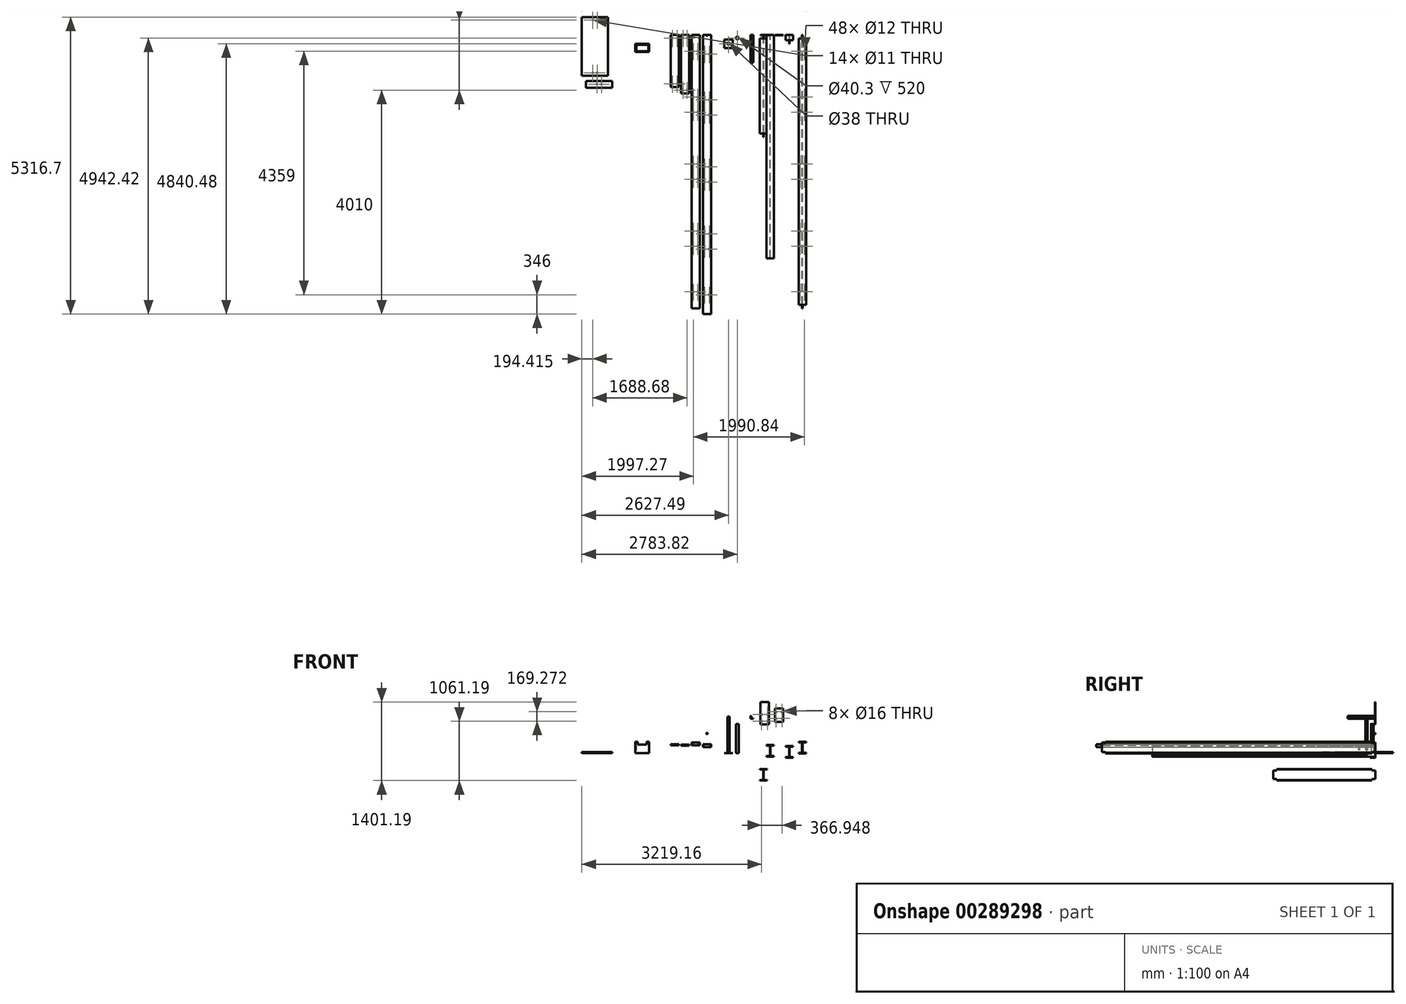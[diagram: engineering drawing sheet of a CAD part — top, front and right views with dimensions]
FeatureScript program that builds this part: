
annotation { "Feature Type Name" : "Feature", "Feature Type Description" : "" }
export const myFeature = defineFeature(function(context is Context, id is Id, definition is map)
    precondition{}
    {
        {
            var Q0;
            Q0=qCreatedBy(makeId("Front.planeOp"),FACE);
            var sketch = newSketch(context, id + "F0", { "sketchPlane" : qUnion([Q0])});
            skLineSegment(sketch, "E0", {"start": v(-21.34, 72.01) * mm, "end": v(112.46, 72.01) * mm});
            skLineSegment(sketch, "E1", {"start": v(-21.34, 72.01) * mm, "end": v(-21.34, 62.41) * mm});
            skLineSegment(sketch, "E2", {"start": v(112.46, 72.01) * mm, "end": v(112.46, 62.41) * mm});
            skLineSegment(sketch, "E3", {"start": v(-21.34, 62.41) * mm, "end": v(42.4, 62.41) * mm});
            skLineSegment(sketch, "E4", {"start": v(112.46, 62.41) * mm, "end": v(48.7, 62.41) * mm});
            skLineSegment(sketch, "E5", {"start": v(42.4, -125.19) * mm, "end": v(-21.34, -125.19) * mm});
            skLineSegment(sketch, "E6", {"start": v(-21.34, -125.19) * mm, "end": v(-21.34, -134.79) * mm});
            skLineSegment(sketch, "E7", {"start": v(-21.34, -134.79) * mm, "end": v(112.46, -134.79) * mm});
            skLineSegment(sketch, "E8", {"start": v(112.46, -134.79) * mm, "end": v(112.46, -125.19) * mm});
            skLineSegment(sketch, "E9", {"start": v(112.46, -125.19) * mm, "end": v(48.7, -125.19) * mm});
            skLineSegment(sketch, "E10", {"start": v(42.4, 62.41) * mm, "end": v(42.4, 54.81) * mm});
            skLineSegment(sketch, "E11", {"start": v(42.4, 54.81) * mm, "end": v(42.4, -117.59) * mm});
            skLineSegment(sketch, "E12", {"start": v(42.4, -117.59) * mm, "end": v(42.4, -125.19) * mm});
            skLineSegment(sketch, "E13", {"start": v(48.7, 62.41) * mm, "end": v(48.7, 54.81) * mm});
            skLineSegment(sketch, "E14", {"start": v(48.7, 54.81) * mm, "end": v(48.7, -117.59) * mm});
            skLineSegment(sketch, "E15", {"start": v(48.7, -117.59) * mm, "end": v(48.7, -125.19) * mm});
            skArc(sketch, "E16", {"start": v(42.4, 54.81) * mm, "mid": v(40.18, 60.19) * mm, "end": v(34.8, 62.41) * mm});
            skArc(sketch, "E17", {"start": v(56.58, 62.41) * mm, "mid": v(51.03, 60.28) * mm, "end": v(48.7, 54.81) * mm});
            skArc(sketch, "E18", {"start": v(42.4, -117.59) * mm, "mid": v(40.18, -122.96) * mm, "end": v(34.8, -125.19) * mm});
            skArc(sketch, "E19", {"start": v(48.7, -117.59) * mm, "mid": v(51.13, -123.16) * mm, "end": v(56.86, -125.19) * mm});
            skLineSegment(sketch, "E20", {"start": v(56.58, 62.41) * mm, "end": v(112.46, 62.41) * mm});
            skSolve(sketch);
        }
        {
            var Q0;
            Q0=qCreatedBy(makeId("Top.planeOp"),FACE);
            var sketch = newSketch(context, id + "F1", { "sketchPlane" : qUnion([Q0])});
            skLineSegment(sketch, "E21.bottom", {"start": v(-453.65, -234.52) * mm, "end": v(-603.65, -234.52) * mm});
            skLineSegment(sketch, "E21.top", {"start": v(-453.65, -84.52) * mm, "end": v(-603.65, -84.52) * mm});
            skLineSegment(sketch, "E21.left", {"start": v(-453.65, -234.52) * mm, "end": v(-453.65, -84.52) * mm});
            skLineSegment(sketch, "E21.right", {"start": v(-603.65, -234.52) * mm, "end": v(-603.65, -84.52) * mm});
            skPoint(sketch, "E21.middle", {"position": v(-528.65, -159.52) * mm});
            skCircle(sketch, "E22", {"center": v(-528.65, -159.52) * mm, "radius": 19 * mm});
            skSolve(sketch);
        }
        {
            var Q0;
            Q0=makeQuery(id+"F1.imprint","IMPRINT",FACE,{"disambiguationData":[TD([[makeQuery(id+"F1.imprint","IMPRINT",EDGE,{"derivedFrom":sQuery(id+"F1.wireOp",EDGE,"E22")}),1.0]])]});
            extrude(context, id + "F2", {"entities" : qUnion([Q0]), "depth" : 650 * mm});
        }
        {
            var Q0;
            Q0=qSketchRegion(id+"F1",true);
            extrude(context, id + "F3", {"entities" : qUnion([Q0]), "oppositeDirection" : true, "depth" : 4 * mm});
        }
        {
            var Q0;
            Q0=qCreatedBy(makeId("Top.planeOp"),FACE);
            var sketch = newSketch(context, id + "F4", { "sketchPlane" : qUnion([Q0])});
            skCircle(sketch, "E23", {"center": v(-372.32, -57.58) * mm, "radius": 24.15 * mm});
            skCircle(sketch, "E24.0", {"center": v(-372.32, -57.58) * mm, "radius": 20.15 * mm});
            skSolve(sketch);
        }
        {
            var Q0;
            Q0=makeQuery(id+"F4.imprint","IMPRINT",FACE,{"disambiguationData":[TD([[makeQuery(id+"F4.imprint","IMPRINT",EDGE,{"derivedFrom":sQuery(id+"F4.wireOp",EDGE,"E23")}),1.0]])]});
            extrude(context, id + "F5", {"entities" : qUnion([Q0]), "depth" : 520 * mm});
        }
        {
            var Q0;
            Q0=makeQuery(id+"F0.imprint","IMPRINT",FACE,{"disambiguationData":[TD([[makeQuery(id+"F0.imprint","IMPRINT",EDGE,{"derivedFrom":sQuery(id+"F0.wireOp",EDGE,"E0")}),-1.0]])]});
            var sketch = newSketch(context, id + "F6", { "sketchPlane" : qUnion([Q0])});
            skLineSegment(sketch, "E25", {"start": v(148.56, 141.3) * mm, "end": v(282.36, 141.3) * mm});
            skLineSegment(sketch, "E26", {"start": v(148.56, 141.3) * mm, "end": v(148.56, 131.7) * mm});
            skLineSegment(sketch, "E27", {"start": v(282.36, 141.3) * mm, "end": v(282.36, 131.7) * mm});
            skLineSegment(sketch, "E28", {"start": v(148.56, 131.7) * mm, "end": v(212.04, 131.7) * mm});
            skLineSegment(sketch, "E29", {"start": v(282.36, 131.7) * mm, "end": v(218.89, 131.7) * mm});
            skLineSegment(sketch, "E30", {"start": v(212.04, -55.9) * mm, "end": v(148.56, -55.9) * mm});
            skLineSegment(sketch, "E31", {"start": v(148.56, -55.9) * mm, "end": v(148.56, -65.5) * mm});
            skLineSegment(sketch, "E32", {"start": v(148.56, -65.5) * mm, "end": v(282.36, -65.5) * mm});
            skLineSegment(sketch, "E33", {"start": v(282.36, -65.5) * mm, "end": v(282.36, -55.9) * mm});
            skLineSegment(sketch, "E34", {"start": v(282.36, -55.9) * mm, "end": v(218.89, -55.9) * mm});
            skLineSegment(sketch, "E35", {"start": v(212.04, 131.7) * mm, "end": v(212.04, 124.1) * mm});
            skLineSegment(sketch, "E36", {"start": v(212.04, 124.1) * mm, "end": v(212.04, -48.3) * mm});
            skLineSegment(sketch, "E37", {"start": v(212.04, -48.3) * mm, "end": v(212.04, -55.9) * mm});
            skLineSegment(sketch, "E38", {"start": v(218.89, 131.7) * mm, "end": v(218.89, 124.1) * mm});
            skLineSegment(sketch, "E39", {"start": v(218.89, 124.1) * mm, "end": v(218.89, -48.3) * mm});
            skLineSegment(sketch, "E40", {"start": v(218.89, -48.3) * mm, "end": v(218.89, -55.9) * mm});
            skArc(sketch, "E41", {"start": v(212.04, 124.1) * mm, "mid": v(209.81, 129.48) * mm, "end": v(204.44, 131.7) * mm});
            skArc(sketch, "E42", {"start": v(226.49, 131.7) * mm, "mid": v(221.11, 129.48) * mm, "end": v(218.89, 124.1) * mm});
            skArc(sketch, "E43", {"start": v(212.04, -48.3) * mm, "mid": v(209.81, -53.67) * mm, "end": v(204.44, -55.9) * mm});
            skArc(sketch, "E44", {"start": v(218.89, -48.3) * mm, "mid": v(221.11, -53.67) * mm, "end": v(226.49, -55.9) * mm});
            skLineSegment(sketch, "E45", {"start": v(226.49, 131.7) * mm, "end": v(282.36, 131.7) * mm});
            skSolve(sketch);
        }
        {
            var Q0;
            Q0=makeQuery(id+"F6.imprint","IMPRINT",FACE,{"disambiguationData":[TD([[makeQuery(id+"F6.imprint","IMPRINT",EDGE,{"derivedFrom":sQuery(id+"F6.wireOp",EDGE,"E25")}),-1.0]])]});
            var Q1;
            {var subQ0=sQuery(id+"F6.wireOp",EDGE,"E40");Q1=makeQuery(id+"F6.imprint","IMPRINT",FACE,{"disambiguationData":[TD([[makeQuery(id+"F6.imprint","IMPRINT",EDGE,{"derivedFrom":subQ0}),1.0]])]});}
            var Q2;
            {var subQ0=sQuery(id+"F6.wireOp",EDGE,"E37");Q2=makeQuery(id+"F6.imprint","IMPRINT",FACE,{"disambiguationData":[TD([[makeQuery(id+"F6.imprint","IMPRINT",EDGE,{"derivedFrom":subQ0}),-1.0]])]});}
            var Q3;
            Q3=makeQuery(id+"F6.imprint","IMPRINT",FACE,{"disambiguationData":[TD([[makeQuery(id+"F6.imprint","IMPRINT",EDGE,{"derivedFrom":sQuery(id+"F6.wireOp",EDGE,"E29")}),1.0]])]});
            var Q4;
            {var subQ0=sQuery(id+"F6.wireOp",EDGE,"E35");Q4=makeQuery(id+"F6.imprint","IMPRINT",FACE,{"disambiguationData":[TD([[makeQuery(id+"F6.imprint","IMPRINT",EDGE,{"derivedFrom":subQ0}),-1.0]])]});}
            extrude(context, id + "F7", {"entities" : qUnion([Q0, Q1, Q2, Q3, Q4]), "depth" : 4000 * mm});
        }
        {
            var Q0;
            Q0=qCreatedBy(makeId("Front.planeOp"),FACE);
            var sketch = newSketch(context, id + "F8", { "sketchPlane" : qUnion([Q0])});
            skLineSegment(sketch, "E46", {"start": v(-125.57, 662.13) * mm, "end": v(-125.57, 620.13) * mm});
            skLineSegment(sketch, "E47", {"start": v(-125.57, 620.13) * mm, "end": v(-83.57, 620.13) * mm});
            skLineSegment(sketch, "E48", {"start": v(-83.57, 620.13) * mm, "end": v(-83.57, 612.13) * mm});
            skLineSegment(sketch, "E49", {"start": v(-83.57, 612.13) * mm, "end": v(-133.57, 612.13) * mm});
            skLineSegment(sketch, "E50", {"start": v(-133.57, 612.13) * mm, "end": v(-133.57, 662.13) * mm});
            skLineSegment(sketch, "E51", {"start": v(-133.57, 662.13) * mm, "end": v(-125.57, 662.13) * mm});
            skSolve(sketch);
        }
        {
            var Q0;
            Q0=makeQuery(id+"F8.imprint","IMPRINT",FACE,{"disambiguationData":[TD([[makeQuery(id+"F8.imprint","IMPRINT",EDGE,{"derivedFrom":sQuery(id+"F8.wireOp",EDGE,"E46")}),-1.0]])]});
            extrude(context, id + "F9", {"entities" : qUnion([Q0]), "depth" : 500 * mm});
        }
        {
            var Q0;
            Q0=qCreatedBy(makeId("Front.planeOp"),FACE);
            var sketch = newSketch(context, id + "F10", { "sketchPlane" : qUnion([Q0])});
            skLineSegment(sketch, "E52", {"start": v(493.4, 124.28) * mm, "end": v(627.2, 124.28) * mm});
            skLineSegment(sketch, "E53", {"start": v(493.4, 124.28) * mm, "end": v(493.4, 114.68) * mm});
            skLineSegment(sketch, "E54", {"start": v(627.2, 124.28) * mm, "end": v(627.2, 114.68) * mm});
            skLineSegment(sketch, "E55", {"start": v(493.4, 114.68) * mm, "end": v(557.15, 114.68) * mm});
            skLineSegment(sketch, "E56", {"start": v(627.2, 114.68) * mm, "end": v(563.45, 114.68) * mm});
            skLineSegment(sketch, "E57", {"start": v(557.15, -72.92) * mm, "end": v(493.4, -72.92) * mm});
            skLineSegment(sketch, "E58", {"start": v(493.4, -72.92) * mm, "end": v(493.4, -82.52) * mm});
            skLineSegment(sketch, "E59", {"start": v(493.4, -82.52) * mm, "end": v(627.2, -82.52) * mm});
            skLineSegment(sketch, "E60", {"start": v(627.2, -82.52) * mm, "end": v(627.2, -72.92) * mm});
            skLineSegment(sketch, "E61", {"start": v(627.2, -72.92) * mm, "end": v(563.45, -72.92) * mm});
            skLineSegment(sketch, "E62", {"start": v(557.15, 114.68) * mm, "end": v(557.15, 107.08) * mm});
            skLineSegment(sketch, "E63", {"start": v(557.15, 107.08) * mm, "end": v(557.15, -65.32) * mm});
            skLineSegment(sketch, "E64", {"start": v(557.15, -65.32) * mm, "end": v(557.15, -72.92) * mm});
            skLineSegment(sketch, "E65", {"start": v(563.45, 114.68) * mm, "end": v(563.45, 107.08) * mm});
            skLineSegment(sketch, "E66", {"start": v(563.45, 107.08) * mm, "end": v(563.45, -65.32) * mm});
            skLineSegment(sketch, "E67", {"start": v(563.45, -65.32) * mm, "end": v(563.45, -72.92) * mm});
            skArc(sketch, "E68", {"start": v(557.15, 107.08) * mm, "mid": v(554.93, 112.46) * mm, "end": v(549.55, 114.68) * mm});
            skArc(sketch, "E69", {"start": v(571.33, 114.68) * mm, "mid": v(565.78, 112.55) * mm, "end": v(563.45, 107.08) * mm});
            skArc(sketch, "E70", {"start": v(557.15, -65.32) * mm, "mid": v(554.93, -70.7) * mm, "end": v(549.55, -72.92) * mm});
            skArc(sketch, "E71", {"start": v(563.45, -65.32) * mm, "mid": v(565.88, -70.89) * mm, "end": v(571.6, -72.92) * mm});
            skLineSegment(sketch, "E72", {"start": v(571.33, 114.68) * mm, "end": v(627.2, 114.68) * mm});
            skSolve(sketch);
        }
        {
            var Q0;
            Q0=makeQuery(id+"F10.imprint","IMPRINT",FACE,{"disambiguationData":[TD([[makeQuery(id+"F10.imprint","IMPRINT",EDGE,{"derivedFrom":sQuery(id+"F10.wireOp",EDGE,"E52")}),-1.0]])]});
            var Q1;
            {var subQ0=sQuery(id+"F10.wireOp",EDGE,"E64");Q1=makeQuery(id+"F10.imprint","IMPRINT",FACE,{"disambiguationData":[TD([[makeQuery(id+"F10.imprint","IMPRINT",EDGE,{"derivedFrom":subQ0}),-1.0]])]});}
            var Q2;
            {var subQ0=sQuery(id+"F10.wireOp",EDGE,"E67");Q2=makeQuery(id+"F10.imprint","IMPRINT",FACE,{"disambiguationData":[TD([[makeQuery(id+"F10.imprint","IMPRINT",EDGE,{"derivedFrom":subQ0}),1.0]])]});}
            var Q3;
            Q3=makeQuery(id+"F10.imprint","IMPRINT",FACE,{"disambiguationData":[TD([[makeQuery(id+"F10.imprint","IMPRINT",EDGE,{"derivedFrom":sQuery(id+"F10.wireOp",EDGE,"E56")}),1.0]])]});
            var Q4;
            {var subQ0=sQuery(id+"F10.wireOp",EDGE,"E62");Q4=makeQuery(id+"F10.imprint","IMPRINT",FACE,{"disambiguationData":[TD([[makeQuery(id+"F10.imprint","IMPRINT",EDGE,{"derivedFrom":subQ0}),-1.0]])]});}
            extrude(context, id + "F11", {"entities" : qUnion([Q0, Q1, Q2, Q3, Q4]), "depth" : 97 * mm});
        }
        {
            var Q0;
            Q0=makeQuery(id+"F11.opExtrude","CAP_FACE",FACE,{"disambiguationData":[OSD([sQuery(id+"F10.wireOp",EDGE,"E52"),sQuery(id+"F10.wireOp",EDGE,"E53"),sQuery(id+"F10.wireOp",EDGE,"E54"),sQuery(id+"F10.wireOp",EDGE,"E55"),sQuery(id+"F10.wireOp",EDGE,"E57"),sQuery(id+"F10.wireOp",EDGE,"E58"),sQuery(id+"F10.wireOp",EDGE,"E59"),sQuery(id+"F10.wireOp",EDGE,"E60"),sQuery(id+"F10.wireOp",EDGE,"E61"),sQuery(id+"F10.wireOp",EDGE,"E63"),sQuery(id+"F10.wireOp",EDGE,"E66"),sQuery(id+"F10.wireOp",EDGE,"E68"),sQuery(id+"F10.wireOp",EDGE,"E69"),sQuery(id+"F10.wireOp",EDGE,"E70"),sQuery(id+"F10.wireOp",EDGE,"E71"),sQuery(id+"F10.wireOp",EDGE,"E72")])],"isStart":false});
            var sketch = newSketch(context, id + "F12", { "sketchPlane" : qUnion([Q0])});
            skLineSegment(sketch, "E73", {"start": v(557.15, 107.08) * mm, "end": v(563.45, 107.08) * mm});
            skLineSegment(sketch, "E74", {"start": v(563.45, 107.08) * mm, "end": v(563.45, -65.32) * mm});
            skLineSegment(sketch, "E75", {"start": v(563.45, -65.32) * mm, "end": v(557.15, -65.32) * mm});
            skLineSegment(sketch, "E76", {"start": v(557.15, -65.32) * mm, "end": v(557.15, 107.08) * mm});
            skSolve(sketch);
        }
        {
            var Q0;
            Q0=qSketchRegion(id+"F12",true);
            extrude(context, id + "F13", {"entities" : qUnion([Q0]), "operationType" : NewBodyOperationType.ADD, "depth" : 64 * mm});
        }
        {
            var Q0;
            Q0=qCreatedBy(makeId("Front.planeOp"),FACE);
            var sketch = newSketch(context, id + "F14", { "sketchPlane" : qUnion([Q0])});
            skLineSegment(sketch, "E77.bottom", {"start": v(42.02, 909.13) * mm, "end": v(192.02, 909.13) * mm});
            skLineSegment(sketch, "E77.top", {"start": v(42.02, 509.13) * mm, "end": v(192.02, 509.13) * mm});
            skLineSegment(sketch, "E77.left", {"start": v(42.02, 909.13) * mm, "end": v(42.02, 509.13) * mm});
            skLineSegment(sketch, "E77.right", {"start": v(192.02, 909.13) * mm, "end": v(192.02, 509.13) * mm});
            skCircle(sketch, "E78", {"center": v(63.02, 689.13) * mm, "radius": 8 * mm});
            skCircle(sketch, "E79", {"center": v(63.02, 569.13) * mm, "radius": 8 * mm});
            skCircle(sketch, "E80", {"center": v(171.02, 689.13) * mm, "radius": 8 * mm});
            skCircle(sketch, "E81", {"center": v(171.02, 569.13) * mm, "radius": 8 * mm});
            skLineSegment(sketch, "E82", {"start": v(171.02, 569.13) * mm, "end": v(63.02, 569.13) * mm, "construction": true});
            skLineSegment(sketch, "E83", {"start": v(171.02, 569.13) * mm, "end": v(171.02, 509.13) * mm, "construction": true});
            skLineSegment(sketch, "E84", {"start": v(63.02, 569.13) * mm, "end": v(63.02, 509.13) * mm});
            skLineSegment(sketch, "E85", {"start": v(63.02, 689.13) * mm, "end": v(171.02, 689.13) * mm, "construction": true});
            skSolve(sketch);
        }
        {
            var Q0;
            Q0=makeQuery(id+"F14.imprint","IMPRINT",FACE,{"disambiguationData":[TD([[makeQuery(id+"F14.imprint","IMPRINT",EDGE,{"derivedFrom":sQuery(id+"F14.wireOp",EDGE,"E77.bottom")}),-1.0]])]});
            extrude(context, id + "F15", {"entities" : qUnion([Q0]), "depth" : 10 * mm});
        }
        {
            var Q0;
            Q0=qCreatedBy(makeId("Front.planeOp"),FACE);
            var sketch = newSketch(context, id + "F16", { "sketchPlane" : qUnion([Q0])});
            skLineSegment(sketch, "E86.bottom", {"start": v(300.96, 798.4) * mm, "end": v(450.96, 798.4) * mm});
            skLineSegment(sketch, "E86.top", {"start": v(300.96, 558.4) * mm, "end": v(450.96, 558.4) * mm});
            skLineSegment(sketch, "E86.left", {"start": v(300.96, 798.4) * mm, "end": v(300.96, 558.4) * mm});
            skLineSegment(sketch, "E86.right", {"start": v(450.96, 798.4) * mm, "end": v(450.96, 558.4) * mm});
            skCircle(sketch, "E87", {"center": v(321.96, 738.4) * mm, "radius": 8 * mm});
            skCircle(sketch, "E88", {"center": v(321.96, 618.4) * mm, "radius": 8 * mm});
            skCircle(sketch, "E89", {"center": v(429.96, 738.4) * mm, "radius": 8 * mm});
            skCircle(sketch, "E90", {"center": v(429.96, 618.4) * mm, "radius": 8 * mm});
            skLineSegment(sketch, "E91", {"start": v(429.96, 618.4) * mm, "end": v(321.96, 618.4) * mm, "construction": true});
            skLineSegment(sketch, "E92", {"start": v(429.96, 618.4) * mm, "end": v(429.96, 558.4) * mm, "construction": true});
            skLineSegment(sketch, "E93", {"start": v(321.96, 618.4) * mm, "end": v(321.96, 558.4) * mm, "construction": true});
            skLineSegment(sketch, "E94", {"start": v(321.96, 738.4) * mm, "end": v(429.96, 738.4) * mm, "construction": true});
            skLineSegment(sketch, "E95", {"start": v(321.96, 738.4) * mm, "end": v(321.96, 618.4) * mm, "construction": true});
            skSolve(sketch);
        }
        {
            var Q0;
            Q0=makeQuery(id+"F16.imprint","IMPRINT",FACE,{"disambiguationData":[TD([[makeQuery(id+"F16.imprint","IMPRINT",EDGE,{"derivedFrom":sQuery(id+"F16.wireOp",EDGE,"E86.bottom")}),-1.0]])]});
            extrude(context, id + "F17", {"entities" : qUnion([Q0]), "depth" : 10 * mm});
        }
        {
            var Q0;
            Q0=qCreatedBy(makeId("Front.planeOp"),FACE);
            var sketch = newSketch(context, id + "F18", { "sketchPlane" : qUnion([Q0])});
            skCircle(sketch, "E96.cCircle", {"center": v(-914.68, 348.98) * mm, "radius": 11.58 * mm, "construction": true});
            skLineSegment(sketch, "E96.0", {"start": v(-901.38, 347.62) * mm, "end": v(-909.2, 336.78) * mm});
            skLineSegment(sketch, "E96.1", {"start": v(-909.2, 336.78) * mm, "end": v(-922.5, 338.14) * mm});
            skLineSegment(sketch, "E96.2", {"start": v(-922.5, 338.14) * mm, "end": v(-927.98, 350.34) * mm});
            skLineSegment(sketch, "E96.3", {"start": v(-927.98, 350.34) * mm, "end": v(-920.15, 361.18) * mm});
            skLineSegment(sketch, "E96.4", {"start": v(-920.15, 361.18) * mm, "end": v(-906.85, 359.82) * mm});
            skLineSegment(sketch, "E96.5", {"start": v(-906.85, 359.82) * mm, "end": v(-901.38, 347.62) * mm});
            skPoint(sketch, "E96.0.midPoint", {"position": v(-905.29, 342.2) * mm});
            skCircle(sketch, "E97", {"center": v(-914.68, 348.98) * mm, "radius": 8 * mm});
            skSolve(sketch);
        }
        {
            var Q0;
            Q0=makeQuery(id+"F18.imprint","IMPRINT",FACE,{"disambiguationData":[TD([[makeQuery(id+"F18.imprint","IMPRINT",EDGE,{"derivedFrom":sQuery(id+"F18.wireOp",EDGE,"E96.0")}),-1.0]])]});
            extrude(context, id + "F19", {"entities" : qUnion([Q0]), "depth" : 14.8 * mm});
        }
        {
            var Q0;
            Q0=qCreatedBy(makeId("Front.planeOp"),FACE);
            var sketch = newSketch(context, id + "F20", { "sketchPlane" : qUnion([Q0])});
            skLineSegment(sketch, "E98.bottom", {"start": v(-989.46, 153.93) * mm, "end": v(-839.46, 153.93) * mm});
            skLineSegment(sketch, "E98.top", {"start": v(-989.46, 106.93) * mm, "end": v(-839.46, 106.93) * mm});
            skLineSegment(sketch, "E98.left", {"start": v(-989.46, 153.93) * mm, "end": v(-989.46, 106.93) * mm});
            skLineSegment(sketch, "E98.right", {"start": v(-839.46, 153.93) * mm, "end": v(-839.46, 106.93) * mm});
            skSolve(sketch);
        }
        {
            var Q0;
            Q0=qSketchRegion(id+"F20",true);
            extrude(context, id + "F21", {"entities" : qUnion([Q0]), "depth" : 5000 * mm});
        }
        {
            var Q0;
            Q0=qCreatedBy(makeId("Front.planeOp"),FACE);
            var sketch = newSketch(context, id + "F22", { "sketchPlane" : qUnion([Q0])});
            skLineSegment(sketch, "E99", {"start": v(725.07, 199.61) * mm, "end": v(858.87, 199.61) * mm});
            skLineSegment(sketch, "E100", {"start": v(725.07, 199.61) * mm, "end": v(725.07, 190.01) * mm});
            skLineSegment(sketch, "E101", {"start": v(858.87, 199.61) * mm, "end": v(858.87, 190.01) * mm});
            skLineSegment(sketch, "E102", {"start": v(725.07, 190.01) * mm, "end": v(788.54, 190.01) * mm});
            skLineSegment(sketch, "E103", {"start": v(858.87, 190.01) * mm, "end": v(795.4, 190.01) * mm});
            skLineSegment(sketch, "E104", {"start": v(788.54, 2.41) * mm, "end": v(725.07, 2.41) * mm});
            skLineSegment(sketch, "E105", {"start": v(725.07, 2.41) * mm, "end": v(725.07, -7.19) * mm});
            skLineSegment(sketch, "E106", {"start": v(725.07, -7.19) * mm, "end": v(858.87, -7.19) * mm});
            skLineSegment(sketch, "E107", {"start": v(858.87, -7.19) * mm, "end": v(858.87, 2.41) * mm});
            skLineSegment(sketch, "E108", {"start": v(858.87, 2.41) * mm, "end": v(795.4, 2.41) * mm});
            skLineSegment(sketch, "E109", {"start": v(788.54, 190.01) * mm, "end": v(788.54, 182.41) * mm});
            skLineSegment(sketch, "E110", {"start": v(788.54, 182.41) * mm, "end": v(788.54, 10.01) * mm});
            skLineSegment(sketch, "E111", {"start": v(788.54, 10.01) * mm, "end": v(788.54, 2.41) * mm});
            skLineSegment(sketch, "E112", {"start": v(795.4, 190.01) * mm, "end": v(795.4, 182.41) * mm});
            skLineSegment(sketch, "E113", {"start": v(795.4, 182.41) * mm, "end": v(795.4, 10.01) * mm});
            skLineSegment(sketch, "E114", {"start": v(795.4, 10.01) * mm, "end": v(795.4, 2.41) * mm});
            skArc(sketch, "E115", {"start": v(788.54, 182.41) * mm, "mid": v(786.32, 187.79) * mm, "end": v(780.94, 190.01) * mm});
            skArc(sketch, "E116", {"start": v(803, 190.01) * mm, "mid": v(797.62, 187.79) * mm, "end": v(795.4, 182.41) * mm});
            skArc(sketch, "E117", {"start": v(788.54, 10.01) * mm, "mid": v(786.32, 4.64) * mm, "end": v(780.94, 2.41) * mm});
            skArc(sketch, "E118", {"start": v(795.4, 10.01) * mm, "mid": v(797.62, 4.64) * mm, "end": v(803, 2.41) * mm});
            skLineSegment(sketch, "E119", {"start": v(803, 190.01) * mm, "end": v(858.87, 190.01) * mm});
            skSolve(sketch);
        }
        {
            var Q0;
            Q0=makeQuery(id+"F22.imprint","IMPRINT",FACE,{"disambiguationData":[TD([[makeQuery(id+"F22.imprint","IMPRINT",EDGE,{"derivedFrom":sQuery(id+"F22.wireOp",EDGE,"E99")}),-1.0]])]});
            var Q1;
            {var subQ0=sQuery(id+"F22.wireOp",EDGE,"E109");Q1=makeQuery(id+"F22.imprint","IMPRINT",FACE,{"disambiguationData":[TD([[makeQuery(id+"F22.imprint","IMPRINT",EDGE,{"derivedFrom":subQ0}),-1.0]])]});}
            var Q2;
            {var subQ0=sQuery(id+"F22.wireOp",EDGE,"E114");Q2=makeQuery(id+"F22.imprint","IMPRINT",FACE,{"disambiguationData":[TD([[makeQuery(id+"F22.imprint","IMPRINT",EDGE,{"derivedFrom":subQ0}),1.0]])]});}
            var Q3;
            Q3=makeQuery(id+"F22.imprint","IMPRINT",FACE,{"disambiguationData":[TD([[makeQuery(id+"F22.imprint","IMPRINT",EDGE,{"derivedFrom":sQuery(id+"F22.wireOp",EDGE,"E103")}),1.0]])]});
            var Q4;
            {var subQ0=sQuery(id+"F22.wireOp",EDGE,"E111");Q4=makeQuery(id+"F22.imprint","IMPRINT",FACE,{"disambiguationData":[TD([[makeQuery(id+"F22.imprint","IMPRINT",EDGE,{"derivedFrom":subQ0}),-1.0]])]});}
            extrude(context, id + "F23", {"entities" : qUnion([Q0, Q1, Q2, Q3, Q4]), "depth" : 4898 * mm});
        }
        {
            var Q0;
            Q0=qCreatedBy(makeId("Front.planeOp"),FACE);
            var sketch = newSketch(context, id + "F24", { "sketchPlane" : qUnion([Q0])});
            skLineSegment(sketch, "E120.bottom", {"start": v(-1383.04, 149.7) * mm, "end": v(-1233.04, 149.7) * mm});
            skLineSegment(sketch, "E120.top", {"start": v(-1383.04, 131.7) * mm, "end": v(-1233.04, 131.7) * mm});
            skLineSegment(sketch, "E120.left", {"start": v(-1383.04, 149.7) * mm, "end": v(-1383.04, 131.7) * mm});
            skLineSegment(sketch, "E120.right", {"start": v(-1233.04, 149.7) * mm, "end": v(-1233.04, 131.7) * mm});
            skSolve(sketch);
        }
        {
            var Q0;
            Q0=makeQuery(id+"F24.imprint","IMPRINT",FACE,{"disambiguationData":[TD([[makeQuery(id+"F24.imprint","IMPRINT",EDGE,{"derivedFrom":sQuery(id+"F24.wireOp",EDGE,"E120.bottom")}),-1.0]])]});
            extrude(context, id + "F25", {"entities" : qUnion([Q0]), "depth" : 1050 * mm});
        }
        {
            var Q0;
            Q0=qCreatedBy(makeId("Front.planeOp"),FACE);
            var sketch = newSketch(context, id + "F26", { "sketchPlane" : qUnion([Q0])});
            skLineSegment(sketch, "E121.bottom", {"start": v(-1566.38, 157.49) * mm, "end": v(-1416.38, 157.49) * mm});
            skLineSegment(sketch, "E121.top", {"start": v(-1566.38, 139.49) * mm, "end": v(-1416.38, 139.49) * mm});
            skLineSegment(sketch, "E121.left", {"start": v(-1566.38, 157.49) * mm, "end": v(-1566.38, 139.49) * mm});
            skLineSegment(sketch, "E121.right", {"start": v(-1416.38, 157.49) * mm, "end": v(-1416.38, 139.49) * mm});
            skSolve(sketch);
        }
        {
            var Q0;
            Q0=makeQuery(id+"F26.imprint","IMPRINT",FACE,{"disambiguationData":[TD([[makeQuery(id+"F26.imprint","IMPRINT",EDGE,{"derivedFrom":sQuery(id+"F26.wireOp",EDGE,"E121.bottom")}),-1.0]])]});
            extrude(context, id + "F27", {"entities" : qUnion([Q0]), "depth" : 939 * mm});
        }
        {
            var Q0;
            Q0=qCreatedBy(makeId("Top.planeOp"),FACE);
            var sketch = newSketch(context, id + "F28", { "sketchPlane" : qUnion([Q0])});
            skLineSegment(sketch, "E122.bottom", {"start": v(-2199.52, -159.74) * mm, "end": v(-1949.52, -159.74) * mm});
            skLineSegment(sketch, "E122.top", {"start": v(-2199.52, -309.74) * mm, "end": v(-1949.52, -309.74) * mm});
            skLineSegment(sketch, "E122.left", {"start": v(-2199.52, -159.74) * mm, "end": v(-2199.52, -309.74) * mm});
            skLineSegment(sketch, "E122.right", {"start": v(-1949.52, -159.74) * mm, "end": v(-1949.52, -309.74) * mm});
            skLineSegment(sketch, "E123.0", {"start": v(-2181.52, -177.74) * mm, "end": v(-1967.52, -177.74) * mm});
            skLineSegment(sketch, "E123.1", {"start": v(-2181.52, -177.74) * mm, "end": v(-2181.52, -291.74) * mm});
            skLineSegment(sketch, "E123.2", {"start": v(-2181.52, -291.74) * mm, "end": v(-1967.52, -291.74) * mm});
            skLineSegment(sketch, "E123.3", {"start": v(-1967.52, -177.74) * mm, "end": v(-1967.52, -291.74) * mm});
            skSolve(sketch);
        }
        {
            var Q0;
            Q0=makeQuery(id+"F28.imprint","IMPRINT",FACE,{"disambiguationData":[TD([[makeQuery(id+"F28.imprint","IMPRINT",EDGE,{"derivedFrom":sQuery(id+"F28.wireOp",EDGE,"E122.bottom")}),-1.0]])]});
            extrude(context, id + "F29", {"entities" : qUnion([Q0]), "depth" : 200 * mm});
        }
        {
            var Q0;
            Q0=makeQuery(id+"F29.opExtrude","SWEPT_FACE",FACE,{"disambiguationData":[OSD([sQuery(id+"F28.wireOp",EDGE,"E122.bottom")])]});
            var sketch = newSketch(context, id + "F30", { "sketchPlane" : qUnion([Q0])});
            skLineSegment(sketch, "E124", {"start": v(2074.52, 200) * mm, "end": v(2074.52, 152.05) * mm});
            skLineSegment(sketch, "E125", {"start": v(2074.52, 152.05) * mm, "end": v(1994.52, 152.05) * mm});
            skLineSegment(sketch, "E126", {"start": v(2074.52, 152.05) * mm, "end": v(2154.52, 152.05) * mm});
            skLineSegment(sketch, "E127", {"start": v(2154.52, 152.05) * mm, "end": v(2154.52, 200) * mm});
            skLineSegment(sketch, "E128", {"start": v(1994.52, 152.05) * mm, "end": v(1994.52, 200) * mm});
            skLineSegment(sketch, "E129", {"start": v(1994.52, 200) * mm, "end": v(2154.52, 200) * mm});
            skSolve(sketch);
        }
        {
            var Q0;
            {var subQ0=sQuery(id+"F30.wireOp",EDGE,"E124");Q0=makeQuery(id+"F30.imprint","IMPRINT",FACE,{"disambiguationData":[TD([[makeQuery(id+"F30.imprint","IMPRINT",EDGE,{"derivedFrom":subQ0}),1.0]])]});}
            var Q1;
            {var subQ0=sQuery(id+"F30.wireOp",EDGE,"E124");Q1=makeQuery(id+"F30.imprint","IMPRINT",FACE,{"disambiguationData":[TD([[makeQuery(id+"F30.imprint","IMPRINT",EDGE,{"derivedFrom":subQ0}),-1.0]])]});}
            extrude(context, id + "F31", {"entities" : qUnion([Q0, Q1]), "operationType" : NewBodyOperationType.REMOVE, "oppositeDirection" : true, "depth" : 150 * mm});
        }
        {
            var Q0;
            Q0=makeQuery(id+"F25.opExtrude","SWEPT_FACE",FACE,{"disambiguationData":[OSD([sQuery(id+"F24.wireOp",EDGE,"E120.bottom")])]});
            var sketch = newSketch(context, id + "F32", { "sketchPlane" : qUnion([Q0])});
            skLineSegment(sketch, "E130", {"start": v(-1308.04, -1050) * mm, "end": v(-1308.04, -990) * mm});
            skLineSegment(sketch, "E131", {"start": v(-1308.04, -990) * mm, "end": v(-1273.04, -990) * mm});
            skLineSegment(sketch, "E132", {"start": v(-1308.04, -990) * mm, "end": v(-1343.04, -990) * mm});
            skLineSegment(sketch, "E133", {"start": v(-1383.04, -525) * mm, "end": v(-1233.04, -525) * mm, "construction": true});
            skLineSegment(sketch, "E134.MirrorCS", {"start": v(-1308.04, 0) * mm, "end": v(-1308.04, -60) * mm});
            skLineSegment(sketch, "E135.MirrorCS", {"start": v(-1308.04, -60) * mm, "end": v(-1273.04, -60) * mm});
            skLineSegment(sketch, "E136.MirrorCS", {"start": v(-1308.04, -60) * mm, "end": v(-1343.04, -60) * mm});
            skCircle(sketch, "E137", {"center": v(-1343.04, -60) * mm, "radius": 11 * mm});
            skSolve(sketch);
        }
        {
            var Q0;
            Q0=sQuery(id+"F32.wireOp",VERTEX,"E136.MirrorCS.end");
            var Q1;
            Q1=sQuery(id+"F32.wireOp",VERTEX,"E135.MirrorCS.end");
            var Q2;
            Q2=sQuery(id+"F32.wireOp",VERTEX,"E132.end");
            var Q3;
            Q3=sQuery(id+"F32.wireOp",VERTEX,"E131.end");
            var Q4;
            Q4=makeQuery(id+"F25.opExtrude","SWEPT_BODY",BODY,{"disambiguationData":[OSD([sQuery(id+"F24.wireOp",EDGE,"E120.bottom"),sQuery(id+"F24.wireOp",EDGE,"E120.top"),sQuery(id+"F24.wireOp",EDGE,"E120.left"),sQuery(id+"F24.wireOp",EDGE,"E120.right")])]});
            hole(context, id + "F33", {"style" : HoleStyle.SIMPLE, "endStyle" : HoleEndStyle.BLIND, "holeDiameter" : 11 * mm, "holeDepth" : 18 * mm, "tappedDepth" : 12 * mm, "tapClearance" : 3, "locations" : qUnion([Q0, Q1, Q2, Q3]), "scope" : qUnion([Q4])});
        }
        {
            var Q0;
            Q0=makeQuery(id+"F23.opExtrude","SWEPT_FACE",FACE,{"disambiguationData":[OSD([sQuery(id+"F22.wireOp",EDGE,"E99")])]});
            var sketch = newSketch(context, id + "F34", { "sketchPlane" : qUnion([Q0])});
            skLineSegment(sketch, "E138", {"start": v(725.07, -2449) * mm, "end": v(858.87, -2449) * mm});
            skLineSegment(sketch, "E139", {"start": v(791.97, -2449) * mm, "end": v(791.97, -2374) * mm});
            skLineSegment(sketch, "E140", {"start": v(791.97, -2374) * mm, "end": v(725.07, -2374) * mm});
            skLineSegment(sketch, "E141", {"start": v(791.97, -2374) * mm, "end": v(858.87, -2374) * mm});
            skLineSegment(sketch, "E142", {"start": v(791.97, -2374) * mm, "end": v(791.97, -2314) * mm});
            skLineSegment(sketch, "E143", {"start": v(791.97, -2314) * mm, "end": v(751.97, -2314) * mm});
            skLineSegment(sketch, "E144", {"start": v(791.97, -2314) * mm, "end": v(831.97, -2314) * mm});
            skLineSegment(sketch, "E145", {"start": v(725.07, -1324) * mm, "end": v(858.87, -1324) * mm});
            skLineSegment(sketch, "E146", {"start": v(791.97, -1324) * mm, "end": v(791.97, -1384) * mm});
            skLineSegment(sketch, "E147", {"start": v(791.97, -1384) * mm, "end": v(831.97, -1384) * mm});
            skLineSegment(sketch, "E148", {"start": v(791.97, -1384) * mm, "end": v(751.97, -1384) * mm});
            skLineSegment(sketch, "E149.top", {"start": v(725.07, -1174) * mm, "end": v(858.87, -1174) * mm});
            skLineSegment(sketch, "E149.left", {"start": v(725.07, -1324) * mm, "end": v(725.07, -1174) * mm});
            skLineSegment(sketch, "E149.right", {"start": v(858.87, -1324) * mm, "end": v(858.87, -1174) * mm});
            skLineSegment(sketch, "E150", {"start": v(725.07, -235) * mm, "end": v(858.87, -235) * mm});
            skLineSegment(sketch, "E151", {"start": v(791.97, -1174) * mm, "end": v(791.97, -1114) * mm});
            skLineSegment(sketch, "E152", {"start": v(791.97, -1114) * mm, "end": v(831.97, -1114) * mm});
            skLineSegment(sketch, "E153", {"start": v(791.97, -1114) * mm, "end": v(751.97, -1114) * mm});
            skLineSegment(sketch, "E154", {"start": v(791.97, -235) * mm, "end": v(791.97, -295) * mm});
            skLineSegment(sketch, "E155", {"start": v(791.97, -295) * mm, "end": v(751.97, -295) * mm});
            skLineSegment(sketch, "E156", {"start": v(791.97, -295) * mm, "end": v(831.97, -295) * mm});
            skLineSegment(sketch, "E157.top", {"start": v(725.07, -85) * mm, "end": v(858.87, -85) * mm});
            skLineSegment(sketch, "E157.left", {"start": v(725.07, -235) * mm, "end": v(725.07, -85) * mm});
            skLineSegment(sketch, "E157.right", {"start": v(858.87, -235) * mm, "end": v(858.87, -85) * mm});
            skLineSegment(sketch, "E158.MirrorCS", {"start": v(791.97, -3724) * mm, "end": v(791.97, -3784) * mm});
            skLineSegment(sketch, "E159.MirrorCS", {"start": v(725.07, -3574) * mm, "end": v(725.07, -3724) * mm});
            skLineSegment(sketch, "E160.MirrorCS", {"start": v(791.97, -3784) * mm, "end": v(831.97, -3784) * mm});
            skLineSegment(sketch, "E161.MirrorCS", {"start": v(791.97, -3574) * mm, "end": v(791.97, -3514) * mm});
            skLineSegment(sketch, "E162.MirrorCS", {"start": v(791.97, -3784) * mm, "end": v(751.97, -3784) * mm});
            skLineSegment(sketch, "E163.MirrorCS", {"start": v(791.97, -2524) * mm, "end": v(791.97, -2584) * mm});
            skLineSegment(sketch, "E164.MirrorCS", {"start": v(791.97, -2449) * mm, "end": v(791.97, -2524) * mm});
            skLineSegment(sketch, "E165.MirrorCS", {"start": v(791.97, -2524) * mm, "end": v(725.07, -2524) * mm});
            skLineSegment(sketch, "E166.MirrorCS", {"start": v(791.97, -3514) * mm, "end": v(831.97, -3514) * mm});
            skLineSegment(sketch, "E167.MirrorCS", {"start": v(725.07, -3574) * mm, "end": v(858.87, -3574) * mm});
            skLineSegment(sketch, "E168.MirrorCS", {"start": v(791.97, -3514) * mm, "end": v(751.97, -3514) * mm});
            skLineSegment(sketch, "E169.MirrorCS", {"start": v(858.87, -3574) * mm, "end": v(858.87, -3724) * mm});
            skLineSegment(sketch, "E170.MirrorCS", {"start": v(791.97, -2584) * mm, "end": v(751.97, -2584) * mm});
            skLineSegment(sketch, "E171.MirrorCS", {"start": v(725.07, -4663) * mm, "end": v(858.87, -4663) * mm});
            skLineSegment(sketch, "E172.MirrorCS", {"start": v(791.97, -2584) * mm, "end": v(831.97, -2584) * mm});
            skLineSegment(sketch, "E173.MirrorCS", {"start": v(791.97, -2524) * mm, "end": v(858.87, -2524) * mm});
            skLineSegment(sketch, "E174.MirrorCS", {"start": v(725.07, -3724) * mm, "end": v(858.87, -3724) * mm});
            skLineSegment(sketch, "E175.MirrorCS", {"start": v(791.97, -4663) * mm, "end": v(791.97, -4603) * mm});
            skLineSegment(sketch, "E176.MirrorCS", {"start": v(791.97, -4603) * mm, "end": v(831.97, -4603) * mm});
            skLineSegment(sketch, "E177.MirrorCS", {"start": v(725.07, -4663) * mm, "end": v(725.07, -4813) * mm});
            skLineSegment(sketch, "E178.MirrorCS", {"start": v(791.97, -4603) * mm, "end": v(751.97, -4603) * mm});
            skLineSegment(sketch, "E179.MirrorCS", {"start": v(858.87, -4663) * mm, "end": v(858.87, -4813) * mm});
            skLineSegment(sketch, "E180.MirrorCS", {"start": v(725.07, -4813) * mm, "end": v(858.87, -4813) * mm});
            skLineSegment(sketch, "E181.bottom", {"start": v(725.07, 0) * mm, "end": v(858.87, 0) * mm});
            skLineSegment(sketch, "E181.top", {"start": v(725.07, -64) * mm, "end": v(858.87, -64) * mm});
            skLineSegment(sketch, "E181.left", {"start": v(725.07, 0) * mm, "end": v(725.07, -64) * mm});
            skLineSegment(sketch, "E181.right", {"start": v(858.87, 0) * mm, "end": v(858.87, -64) * mm});
            skLineSegment(sketch, "E182.MirrorCS", {"start": v(725.07, -4834) * mm, "end": v(858.87, -4834) * mm});
            skLineSegment(sketch, "E183.MirrorCS", {"start": v(725.07, -4898) * mm, "end": v(725.07, -4834) * mm});
            skLineSegment(sketch, "E184.MirrorCS", {"start": v(725.07, -4898) * mm, "end": v(858.87, -4898) * mm});
            skLineSegment(sketch, "E185.MirrorCS", {"start": v(858.87, -4898) * mm, "end": v(858.87, -4834) * mm});
            skSolve(sketch);
        }
        {
            var Q0;
            Q0=sQuery(id+"F34.wireOp",VERTEX,"E155.end");
            var Q1;
            Q1=sQuery(id+"F34.wireOp",VERTEX,"E156.end");
            var Q2;
            Q2=sQuery(id+"F34.wireOp",VERTEX,"E153.end");
            var Q3;
            Q3=sQuery(id+"F34.wireOp",VERTEX,"E152.end");
            var Q4;
            Q4=sQuery(id+"F34.wireOp",VERTEX,"E148.end");
            var Q5;
            Q5=sQuery(id+"F34.wireOp",VERTEX,"E147.end");
            var Q6;
            Q6=sQuery(id+"F34.wireOp",VERTEX,"E143.end");
            var Q7;
            Q7=sQuery(id+"F34.wireOp",VERTEX,"E144.end");
            var Q8;
            Q8=sQuery(id+"F34.wireOp",VERTEX,"E170.MirrorCS.end");
            var Q9;
            Q9=sQuery(id+"F34.wireOp",VERTEX,"E172.MirrorCS.end");
            var Q10;
            Q10=sQuery(id+"F34.wireOp",VERTEX,"E168.MirrorCS.end");
            var Q11;
            Q11=sQuery(id+"F34.wireOp",VERTEX,"E166.MirrorCS.end");
            var Q12;
            Q12=sQuery(id+"F34.wireOp",VERTEX,"E162.MirrorCS.end");
            var Q13;
            Q13=sQuery(id+"F34.wireOp",VERTEX,"E160.MirrorCS.end");
            var Q14;
            Q14=sQuery(id+"F34.wireOp",VERTEX,"E178.MirrorCS.end");
            var Q15;
            Q15=sQuery(id+"F34.wireOp",VERTEX,"E176.MirrorCS.end");
            var Q16;
            Q16=makeQuery(id+"F23.opExtrude","SWEPT_BODY",BODY,{"disambiguationData":[OSD([sQuery(id+"F22.wireOp",EDGE,"E99"),sQuery(id+"F22.wireOp",EDGE,"E100"),sQuery(id+"F22.wireOp",EDGE,"E101"),sQuery(id+"F22.wireOp",EDGE,"E102"),sQuery(id+"F22.wireOp",EDGE,"E104"),sQuery(id+"F22.wireOp",EDGE,"E105"),sQuery(id+"F22.wireOp",EDGE,"E106"),sQuery(id+"F22.wireOp",EDGE,"E107"),sQuery(id+"F22.wireOp",EDGE,"E108"),sQuery(id+"F22.wireOp",EDGE,"E110"),sQuery(id+"F22.wireOp",EDGE,"E113"),sQuery(id+"F22.wireOp",EDGE,"E115"),sQuery(id+"F22.wireOp",EDGE,"E116"),sQuery(id+"F22.wireOp",EDGE,"E117"),sQuery(id+"F22.wireOp",EDGE,"E118"),sQuery(id+"F22.wireOp",EDGE,"E119")])]});
            hole(context, id + "F35", {"style" : HoleStyle.SIMPLE, "endStyle" : HoleEndStyle.BLIND, "holeDiameter" : 12 * mm, "holeDepth" : 10 * mm, "tappedDepth" : 12 * mm, "tapClearance" : 3, "locations" : qUnion([Q0, Q1, Q2, Q3, Q4, Q5, Q6, Q7, Q8, Q9, Q10, Q11, Q12, Q13, Q14, Q15]), "scope" : qUnion([Q16])});
        }
        {
            var Q0;
            Q0=makeQuery(id+"F27.opExtrude","SWEPT_FACE",FACE,{"disambiguationData":[OSD([sQuery(id+"F26.wireOp",EDGE,"E121.bottom")])]});
            var sketch = newSketch(context, id + "F36", { "sketchPlane" : qUnion([Q0])});
            skLineSegment(sketch, "E186", {"start": v(-1491.38, 0) * mm, "end": v(-1491.38, -60) * mm});
            skLineSegment(sketch, "E187", {"start": v(-1491.38, -60) * mm, "end": v(-1451.38, -60) * mm});
            skLineSegment(sketch, "E188", {"start": v(-1566.38, -469.5) * mm, "end": v(-1416.38, -469.5) * mm});
            skLineSegment(sketch, "E189", {"start": v(-1491.38, -60) * mm, "end": v(-1531.38, -60) * mm});
            skLineSegment(sketch, "E190.MirrorCS", {"start": v(-1491.38, -879) * mm, "end": v(-1451.38, -879) * mm});
            skLineSegment(sketch, "E191.MirrorCS", {"start": v(-1491.38, -879) * mm, "end": v(-1531.38, -879) * mm});
            skLineSegment(sketch, "E192.MirrorCS", {"start": v(-1491.38, -939) * mm, "end": v(-1491.38, -879) * mm});
            skSolve(sketch);
        }
        {
            var Q0;
            Q0=sQuery(id+"F36.wireOp",VERTEX,"E189.end");
            var Q1;
            Q1=sQuery(id+"F36.wireOp",VERTEX,"E187.end");
            var Q2;
            Q2=sQuery(id+"F36.wireOp",VERTEX,"E191.MirrorCS.end");
            var Q3;
            Q3=sQuery(id+"F36.wireOp",VERTEX,"E190.MirrorCS.end");
            var Q4;
            Q4=makeQuery(id+"F27.opExtrude","SWEPT_BODY",BODY,{"disambiguationData":[OSD([sQuery(id+"F26.wireOp",EDGE,"E121.bottom"),sQuery(id+"F26.wireOp",EDGE,"E121.top"),sQuery(id+"F26.wireOp",EDGE,"E121.left"),sQuery(id+"F26.wireOp",EDGE,"E121.right")])]});
            hole(context, id + "F37", {"style" : HoleStyle.SIMPLE, "endStyle" : HoleEndStyle.BLIND, "holeDiameter" : 11 * mm, "holeDepth" : 18 * mm, "tappedDepth" : 12 * mm, "tapClearance" : 3, "locations" : qUnion([Q0, Q1, Q2, Q3]), "scope" : qUnion([Q4])});
        }
        {
            var Q0;
            Q0=qCreatedBy(makeId("Front.planeOp"),FACE);
            var sketch = newSketch(context, id + "F38", { "sketchPlane" : qUnion([Q0])});
            skLineSegment(sketch, "E193.bottom", {"start": v(-1191.37, 185.27) * mm, "end": v(-1046.37, 185.27) * mm});
            skLineSegment(sketch, "E193.top", {"start": v(-1191.37, 140.27) * mm, "end": v(-1046.37, 140.27) * mm});
            skLineSegment(sketch, "E193.left", {"start": v(-1191.37, 185.27) * mm, "end": v(-1191.37, 140.27) * mm});
            skLineSegment(sketch, "E193.right", {"start": v(-1046.37, 185.27) * mm, "end": v(-1046.37, 140.27) * mm});
            skSolve(sketch);
        }
        {
            var Q0;
            Q0=makeQuery(id+"F38.imprint","IMPRINT",FACE,{"disambiguationData":[TD([[makeQuery(id+"F38.imprint","IMPRINT",EDGE,{"derivedFrom":sQuery(id+"F38.wireOp",EDGE,"E193.bottom")}),-1.0]])]});
            extrude(context, id + "F39", {"entities" : qUnion([Q0]), "depth" : 4898 * mm});
        }
        {
            var Q0;
            Q0=makeQuery(id+"F21.opExtrude","SWEPT_FACE",FACE,{"disambiguationData":[OSD([sQuery(id+"F20.wireOp",EDGE,"E98.bottom")])]});
            var sketch = newSketch(context, id + "F40", { "sketchPlane" : qUnion([Q0])});
            skLineSegment(sketch, "E194", {"start": v(-989.46, -2500) * mm, "end": v(-839.46, -2500) * mm});
            skLineSegment(sketch, "E195", {"start": v(-914.46, -2500) * mm, "end": v(-914.46, -2365) * mm});
            skLineSegment(sketch, "E196", {"start": v(-914.46, -2365) * mm, "end": v(-914.46, -1435) * mm});
            skLineSegment(sketch, "E197", {"start": v(-914.46, -1435) * mm, "end": v(-914.46, -1165) * mm});
            skLineSegment(sketch, "E198", {"start": v(-914.46, -1165) * mm, "end": v(-914.46, -346) * mm});
            skLineSegment(sketch, "E199", {"start": v(-914.46, -2365) * mm, "end": v(-954.46, -2365) * mm});
            skLineSegment(sketch, "E200", {"start": v(-914.46, -1435) * mm, "end": v(-954.46, -1435) * mm});
            skLineSegment(sketch, "E201", {"start": v(-914.46, -1165) * mm, "end": v(-954.46, -1165) * mm});
            skLineSegment(sketch, "E202", {"start": v(-914.46, -346) * mm, "end": v(-954.46, -346) * mm});
            skLineSegment(sketch, "E203.MirrorCS", {"start": v(-914.46, -1435) * mm, "end": v(-874.46, -1435) * mm});
            skLineSegment(sketch, "E204.MirrorCS", {"start": v(-914.46, -2365) * mm, "end": v(-874.46, -2365) * mm});
            skLineSegment(sketch, "E205.MirrorCS", {"start": v(-914.46, -1165) * mm, "end": v(-874.46, -1165) * mm});
            skLineSegment(sketch, "E206.MirrorCS", {"start": v(-914.46, -346) * mm, "end": v(-874.46, -346) * mm});
            skLineSegment(sketch, "E207.MirrorCS", {"start": v(-914.46, -3565) * mm, "end": v(-914.46, -3835) * mm});
            skLineSegment(sketch, "E208.MirrorCS", {"start": v(-914.46, -2635) * mm, "end": v(-914.46, -3565) * mm});
            skLineSegment(sketch, "E209.MirrorCS", {"start": v(-914.46, -3565) * mm, "end": v(-874.46, -3565) * mm});
            skLineSegment(sketch, "E210.MirrorCS", {"start": v(-914.46, -2635) * mm, "end": v(-874.46, -2635) * mm});
            skLineSegment(sketch, "E211.MirrorCS", {"start": v(-914.46, -4654) * mm, "end": v(-874.46, -4654) * mm});
            skLineSegment(sketch, "E212.MirrorCS", {"start": v(-914.46, -3835) * mm, "end": v(-874.46, -3835) * mm});
            skLineSegment(sketch, "E213.MirrorCS", {"start": v(-914.46, -3835) * mm, "end": v(-914.46, -4654) * mm});
            skLineSegment(sketch, "E214.MirrorCS", {"start": v(-914.46, -3565) * mm, "end": v(-954.46, -3565) * mm});
            skLineSegment(sketch, "E215.MirrorCS", {"start": v(-914.46, -3835) * mm, "end": v(-954.46, -3835) * mm});
            skLineSegment(sketch, "E216.MirrorCS", {"start": v(-914.46, -4654) * mm, "end": v(-954.46, -4654) * mm});
            skLineSegment(sketch, "E217", {"start": v(-914.46, -2635) * mm, "end": v(-954.46, -2635) * mm});
            skSolve(sketch);
        }
        {
            var Q0;
            Q0=sQuery(id+"F40.wireOp",VERTEX,"E202.end");
            var Q1;
            Q1=sQuery(id+"F40.wireOp",VERTEX,"E206.MirrorCS.end");
            var Q2;
            Q2=sQuery(id+"F40.wireOp",VERTEX,"E201.end");
            var Q3;
            Q3=sQuery(id+"F40.wireOp",VERTEX,"E205.MirrorCS.end");
            var Q4;
            Q4=sQuery(id+"F40.wireOp",VERTEX,"E200.end");
            var Q5;
            Q5=sQuery(id+"F40.wireOp",VERTEX,"E203.MirrorCS.end");
            var Q6;
            Q6=sQuery(id+"F40.wireOp",VERTEX,"E199.end");
            var Q7;
            Q7=sQuery(id+"F40.wireOp",VERTEX,"E204.MirrorCS.end");
            var Q8;
            Q8=sQuery(id+"F40.wireOp",VERTEX,"E217.end");
            var Q9;
            Q9=sQuery(id+"F40.wireOp",VERTEX,"E210.MirrorCS.end");
            var Q10;
            Q10=sQuery(id+"F40.wireOp",VERTEX,"E214.MirrorCS.end");
            var Q11;
            Q11=sQuery(id+"F40.wireOp",VERTEX,"E209.MirrorCS.end");
            var Q12;
            Q12=sQuery(id+"F40.wireOp",VERTEX,"E215.MirrorCS.end");
            var Q13;
            Q13=sQuery(id+"F40.wireOp",VERTEX,"E212.MirrorCS.end");
            var Q14;
            Q14=sQuery(id+"F40.wireOp",VERTEX,"E216.MirrorCS.end");
            var Q15;
            Q15=sQuery(id+"F40.wireOp",VERTEX,"E211.MirrorCS.end");
            var Q16;
            Q16=makeQuery(id+"F21.opExtrude","SWEPT_BODY",BODY,{"disambiguationData":[OSD([sQuery(id+"F20.wireOp",EDGE,"E98.bottom"),sQuery(id+"F20.wireOp",EDGE,"E98.top"),sQuery(id+"F20.wireOp",EDGE,"E98.left"),sQuery(id+"F20.wireOp",EDGE,"E98.right")])]});
            hole(context, id + "F41", {"style" : HoleStyle.SIMPLE, "endStyle" : HoleEndStyle.BLIND, "holeDiameter" : 12 * mm, "holeDepth" : 10 * mm, "tappedDepth" : 12 * mm, "tapClearance" : 3, "locations" : qUnion([Q0, Q1, Q2, Q3, Q4, Q5, Q6, Q7, Q8, Q9, Q10, Q11, Q12, Q13, Q14, Q15]), "scope" : qUnion([Q16])});
        }
        {
            var Q0;
            Q0=makeQuery(id+"F39.opExtrude","SWEPT_FACE",FACE,{"disambiguationData":[OSD([sQuery(id+"F38.wireOp",EDGE,"E193.bottom")])]});
            var sketch = newSketch(context, id + "F42", { "sketchPlane" : qUnion([Q0])});
            skLineSegment(sketch, "E218", {"start": v(-1191.37, -2449) * mm, "end": v(-1046.37, -2449) * mm});
            skLineSegment(sketch, "E219", {"start": v(-1118.87, -2449) * mm, "end": v(-1118.87, -2314) * mm});
            skLineSegment(sketch, "E220", {"start": v(-1118.87, -2314) * mm, "end": v(-1158.87, -2314) * mm});
            skLineSegment(sketch, "E221", {"start": v(-1118.87, -2314) * mm, "end": v(-1118.87, -1384) * mm});
            skLineSegment(sketch, "E222", {"start": v(-1118.87, -1384) * mm, "end": v(-1158.87, -1384) * mm});
            skLineSegment(sketch, "E223", {"start": v(-1118.87, -1384) * mm, "end": v(-1118.87, -1114) * mm});
            skLineSegment(sketch, "E224", {"start": v(-1118.87, -1114) * mm, "end": v(-1118.87, -295) * mm});
            skLineSegment(sketch, "E225", {"start": v(-1118.87, -295) * mm, "end": v(-1158.87, -295) * mm});
            skLineSegment(sketch, "E226.MirrorCS", {"start": v(-1118.87, -295) * mm, "end": v(-1078.87, -295) * mm});
            skLineSegment(sketch, "E227.MirrorCS", {"start": v(-1118.87, -1384) * mm, "end": v(-1078.87, -1384) * mm});
            skLineSegment(sketch, "E228.MirrorCS", {"start": v(-1118.87, -2314) * mm, "end": v(-1078.87, -2314) * mm});
            skLineSegment(sketch, "E229.MirrorCS", {"start": v(-1118.87, -2584) * mm, "end": v(-1158.87, -2584) * mm});
            skLineSegment(sketch, "E230.MirrorCS", {"start": v(-1118.87, -4603) * mm, "end": v(-1158.87, -4603) * mm});
            skLineSegment(sketch, "E231.MirrorCS", {"start": v(-1118.87, -4603) * mm, "end": v(-1078.87, -4603) * mm});
            skLineSegment(sketch, "E232.MirrorCS", {"start": v(-1118.87, -2584) * mm, "end": v(-1078.87, -2584) * mm});
            skLineSegment(sketch, "E233.MirrorCS", {"start": v(-1118.87, -2584) * mm, "end": v(-1118.87, -3514) * mm});
            skLineSegment(sketch, "E234.MirrorCS", {"start": v(-1118.87, -3514) * mm, "end": v(-1118.87, -3784) * mm});
            skLineSegment(sketch, "E235.MirrorCS", {"start": v(-1118.87, -3514) * mm, "end": v(-1078.87, -3514) * mm});
            skLineSegment(sketch, "E236.MirrorCS", {"start": v(-1118.87, -3514) * mm, "end": v(-1158.87, -3514) * mm});
            skLineSegment(sketch, "E237.MirrorCS", {"start": v(-1118.87, -3784) * mm, "end": v(-1118.87, -4603) * mm});
            skLineSegment(sketch, "E238", {"start": v(-1118.87, -1114) * mm, "end": v(-1078.87, -1114) * mm});
            skLineSegment(sketch, "E239", {"start": v(-1118.87, -1114) * mm, "end": v(-1158.87, -1114) * mm});
            skLineSegment(sketch, "E240", {"start": v(-1118.87, -3784) * mm, "end": v(-1078.87, -3784) * mm});
            skLineSegment(sketch, "E241", {"start": v(-1118.87, -3784) * mm, "end": v(-1158.87, -3784) * mm});
            skSolve(sketch);
        }
        {
            var Q0;
            Q0=sQuery(id+"F42.wireOp",VERTEX,"E225.end");
            var Q1;
            Q1=sQuery(id+"F42.wireOp",VERTEX,"E226.MirrorCS.end");
            var Q2;
            Q2=sQuery(id+"F42.wireOp",VERTEX,"E239.end");
            var Q3;
            Q3=sQuery(id+"F42.wireOp",VERTEX,"E238.end");
            var Q4;
            Q4=sQuery(id+"F42.wireOp",VERTEX,"E222.end");
            var Q5;
            Q5=sQuery(id+"F42.wireOp",VERTEX,"E227.MirrorCS.end");
            var Q6;
            Q6=sQuery(id+"F42.wireOp",VERTEX,"E220.end");
            var Q7;
            Q7=sQuery(id+"F42.wireOp",VERTEX,"E228.MirrorCS.end");
            var Q8;
            Q8=sQuery(id+"F42.wireOp",VERTEX,"E229.MirrorCS.end");
            var Q9;
            Q9=sQuery(id+"F42.wireOp",VERTEX,"E232.MirrorCS.end");
            var Q10;
            Q10=sQuery(id+"F42.wireOp",VERTEX,"E236.MirrorCS.end");
            var Q11;
            Q11=sQuery(id+"F42.wireOp",VERTEX,"E235.MirrorCS.end");
            var Q12;
            Q12=sQuery(id+"F42.wireOp",VERTEX,"E241.end");
            var Q13;
            Q13=sQuery(id+"F42.wireOp",VERTEX,"E240.end");
            var Q14;
            Q14=sQuery(id+"F42.wireOp",VERTEX,"E230.MirrorCS.end");
            var Q15;
            Q15=sQuery(id+"F42.wireOp",VERTEX,"E231.MirrorCS.end");
            var Q16;
            Q16=makeQuery(id+"F39.opExtrude","SWEPT_BODY",BODY,{"disambiguationData":[OSD([sQuery(id+"F38.wireOp",EDGE,"E193.bottom"),sQuery(id+"F38.wireOp",EDGE,"E193.top"),sQuery(id+"F38.wireOp",EDGE,"E193.left"),sQuery(id+"F38.wireOp",EDGE,"E193.right")])]});
            hole(context, id + "F43", {"style" : HoleStyle.SIMPLE, "endStyle" : HoleEndStyle.BLIND, "holeDiameter" : 12 * mm, "holeDepth" : 45 * mm, "tappedDepth" : 12 * mm, "tapClearance" : 3, "locations" : qUnion([Q0, Q1, Q2, Q3, Q4, Q5, Q6, Q7, Q8, Q9, Q10, Q11, Q12, Q13, Q14, Q15]), "scope" : qUnion([Q16])});
        }
        {
            var Q0;
            Q0=qCreatedBy(makeId("Top.planeOp"),FACE);
            var sketch = newSketch(context, id + "F44", { "sketchPlane" : qUnion([Q0])});
            skLineSegment(sketch, "E242.bottom", {"start": v(-3156.14, 316.7) * mm, "end": v(-2687.3, 316.7) * mm});
            skLineSegment(sketch, "E242.top", {"start": v(-3156.14, -733.3) * mm, "end": v(-2687.3, -733.3) * mm});
            skLineSegment(sketch, "E242.left", {"start": v(-3156.14, 316.7) * mm, "end": v(-3156.14, -733.3) * mm});
            skLineSegment(sketch, "E242.right", {"start": v(-2687.3, 316.7) * mm, "end": v(-2687.3, -733.3) * mm});
            skLineSegment(sketch, "E243", {"start": v(-2921.73, 316.7) * mm, "end": v(-2921.73, 256.7) * mm});
            skLineSegment(sketch, "E244", {"start": v(-2921.73, 256.7) * mm, "end": v(-2961.73, 256.7) * mm});
            skLineSegment(sketch, "E245", {"start": v(-2921.73, 256.7) * mm, "end": v(-2881.73, 256.7) * mm});
            skLineSegment(sketch, "E246", {"start": v(-3156.14, -208.3) * mm, "end": v(-2687.3, -208.3) * mm, "construction": true});
            skLineSegment(sketch, "E247.MirrorCS", {"start": v(-2921.73, -673.3) * mm, "end": v(-2881.73, -673.3) * mm});
            skLineSegment(sketch, "E248.MirrorCS", {"start": v(-2921.73, -673.3) * mm, "end": v(-2961.73, -673.3) * mm});
            skLineSegment(sketch, "E249.MirrorCS", {"start": v(-2921.73, -733.3) * mm, "end": v(-2921.73, -673.3) * mm});
            skSolve(sketch);
        }
        {
            var Q0;
            {var subQ3=sQuery(id+"F44.wireOp",EDGE,"E242.left");Q0=makeQuery(id+"F44.imprint","IMPRINT",FACE,{"disambiguationData":[TD([[makeQuery(id+"F44.imprint","IMPRINT",EDGE,{"derivedFrom":subQ3}),1.0]])]});}
            extrude(context, id + "F45", {"entities" : qUnion([Q0]), "depth" : 18 * mm});
        }
        {
            var Q0;
            Q0=makeQuery(id+"F45.opExtrude","CAP_FACE",FACE,{"disambiguationData":[OSD([sQuery(id+"F44.wireOp",EDGE,"E242.bottom"),sQuery(id+"F44.wireOp",EDGE,"E242.top"),sQuery(id+"F44.wireOp",EDGE,"E242.left"),sQuery(id+"F44.wireOp",EDGE,"E242.right")])],"isStart":false});
            var sketch = newSketch(context, id + "F46", { "sketchPlane" : qUnion([Q0])});
            skLineSegment(sketch, "E250", {"start": v(-2921.73, -733.3) * mm, "end": v(-2921.73, -679.57) * mm});
            skLineSegment(sketch, "E251", {"start": v(-2921.73, -679.57) * mm, "end": v(-2961.73, -679.57) * mm});
            skLineSegment(sketch, "E252", {"start": v(-2921.73, -679.57) * mm, "end": v(-2881.73, -679.57) * mm});
            skLineSegment(sketch, "E253", {"start": v(-2687.3, -208.3) * mm, "end": v(-3156.14, -208.3) * mm, "construction": true});
            skLineSegment(sketch, "E254.MirrorCS", {"start": v(-2921.73, 262.98) * mm, "end": v(-2881.73, 262.98) * mm});
            skLineSegment(sketch, "E255.MirrorCS", {"start": v(-2921.73, 316.7) * mm, "end": v(-2921.73, 262.98) * mm});
            skLineSegment(sketch, "E256.MirrorCS", {"start": v(-2921.73, 262.98) * mm, "end": v(-2961.73, 262.98) * mm});
            skSolve(sketch);
        }
        {
            var Q0;
            Q0=sQuery(id+"F46.wireOp",VERTEX,"E252.end");
            var Q1;
            Q1=sQuery(id+"F46.wireOp",VERTEX,"E251.end");
            var Q2;
            Q2=sQuery(id+"F46.wireOp",VERTEX,"E254.MirrorCS.end");
            var Q3;
            Q3=sQuery(id+"F46.wireOp",VERTEX,"E256.MirrorCS.end");
            var Q4;
            Q4=makeQuery(id+"F45.opExtrude","SWEPT_BODY",BODY,{"disambiguationData":[OSD([sQuery(id+"F44.wireOp",EDGE,"E242.bottom"),sQuery(id+"F44.wireOp",EDGE,"E242.top"),sQuery(id+"F44.wireOp",EDGE,"E242.left"),sQuery(id+"F44.wireOp",EDGE,"E242.right")])]});
            hole(context, id + "F47", {"style" : HoleStyle.SIMPLE, "endStyle" : HoleEndStyle.BLIND, "holeDiameter" : 11 * mm, "holeDepth" : 18 * mm, "tappedDepth" : 12 * mm, "tapClearance" : 3, "locations" : qUnion([Q0, Q1, Q2, Q3]), "scope" : qUnion([Q4])});
        }
        {
            var Q0;
            Q0=qCreatedBy(makeId("Top.planeOp"),FACE);
            var sketch = newSketch(context, id + "F48", { "sketchPlane" : qUnion([Q0])});
            skLineSegment(sketch, "E257.bottom", {"start": v(-3079.15, -826.54) * mm, "end": v(-2610.51, -826.54) * mm});
            skLineSegment(sketch, "E257.top", {"start": v(-3079.15, -946.54) * mm, "end": v(-2610.51, -946.54) * mm});
            skLineSegment(sketch, "E257.left", {"start": v(-3079.15, -826.54) * mm, "end": v(-3079.15, -946.54) * mm});
            skLineSegment(sketch, "E257.right", {"start": v(-2610.51, -826.54) * mm, "end": v(-2610.51, -946.54) * mm});
            skSolve(sketch);
        }
        {
            var Q0;
            Q0=makeQuery(id+"F48.imprint","IMPRINT",FACE,{"disambiguationData":[TD([[makeQuery(id+"F48.imprint","IMPRINT",EDGE,{"derivedFrom":sQuery(id+"F48.wireOp",EDGE,"E257.bottom")}),-1.0]])]});
            extrude(context, id + "F49", {"entities" : qUnion([Q0]), "depth" : 18 * mm});
        }
        {
            var Q0;
            Q0=makeQuery(id+"F49.opExtrude","CAP_FACE",FACE,{"disambiguationData":[OSD([sQuery(id+"F48.wireOp",EDGE,"E257.bottom"),sQuery(id+"F48.wireOp",EDGE,"E257.top"),sQuery(id+"F48.wireOp",EDGE,"E257.left"),sQuery(id+"F48.wireOp",EDGE,"E257.right")])],"isStart":false});
            var sketch = newSketch(context, id + "F50", { "sketchPlane" : qUnion([Q0])});
            skLineSegment(sketch, "E258", {"start": v(-2844.83, -826.54) * mm, "end": v(-2844.83, -886.54) * mm});
            skPoint(sketch, "E258.endSnap0", {"position": v(-2844.83, -946.54) * mm});
            skLineSegment(sketch, "E259", {"start": v(-2844.83, -886.54) * mm, "end": v(-2884.83, -886.54) * mm});
            skLineSegment(sketch, "E260", {"start": v(-2844.83, -886.54) * mm, "end": v(-2804.83, -886.54) * mm});
            skSolve(sketch);
        }
        {
            var Q0;
            Q0=sQuery(id+"F50.wireOp",VERTEX,"E259.end");
            var Q1;
            Q1=sQuery(id+"F50.wireOp",VERTEX,"E260.end");
            var Q2;
            Q2=makeQuery(id+"F49.opExtrude","SWEPT_BODY",BODY,{"disambiguationData":[OSD([sQuery(id+"F48.wireOp",EDGE,"E257.bottom"),sQuery(id+"F48.wireOp",EDGE,"E257.top"),sQuery(id+"F48.wireOp",EDGE,"E257.left"),sQuery(id+"F48.wireOp",EDGE,"E257.right")])]});
            hole(context, id + "F51", {"style" : HoleStyle.SIMPLE, "endStyle" : HoleEndStyle.BLIND, "holeDiameter" : 11 * mm, "holeDepth" : 18 * mm, "tappedDepth" : 12 * mm, "tapClearance" : 3, "locations" : qUnion([Q0, Q1]), "scope" : qUnion([Q2])});
        }
        {
            var Q0;
            Q0=qCreatedBy(makeId("Front.planeOp"),FACE);
            var sketch = newSketch(context, id + "F52", { "sketchPlane" : qUnion([Q0])});
            skLineSegment(sketch, "E261", {"start": v(29.87, -285.26) * mm, "end": v(163.67, -285.26) * mm});
            skLineSegment(sketch, "E262", {"start": v(29.87, -285.26) * mm, "end": v(29.87, -294.86) * mm});
            skLineSegment(sketch, "E263", {"start": v(163.67, -285.26) * mm, "end": v(163.67, -294.86) * mm});
            skLineSegment(sketch, "E264", {"start": v(29.87, -294.86) * mm, "end": v(93.62, -294.86) * mm});
            skLineSegment(sketch, "E265", {"start": v(163.67, -294.86) * mm, "end": v(99.92, -294.86) * mm});
            skLineSegment(sketch, "E266", {"start": v(93.62, -482.46) * mm, "end": v(29.87, -482.46) * mm});
            skLineSegment(sketch, "E267", {"start": v(29.87, -482.46) * mm, "end": v(29.87, -492.06) * mm});
            skLineSegment(sketch, "E268", {"start": v(29.87, -492.06) * mm, "end": v(163.67, -492.06) * mm});
            skLineSegment(sketch, "E269", {"start": v(163.67, -492.06) * mm, "end": v(163.67, -482.46) * mm});
            skLineSegment(sketch, "E270", {"start": v(163.67, -482.46) * mm, "end": v(99.92, -482.46) * mm});
            skLineSegment(sketch, "E271", {"start": v(93.62, -294.86) * mm, "end": v(93.62, -302.46) * mm});
            skLineSegment(sketch, "E272", {"start": v(93.62, -302.46) * mm, "end": v(93.62, -474.86) * mm});
            skLineSegment(sketch, "E273", {"start": v(93.62, -474.86) * mm, "end": v(93.62, -482.46) * mm});
            skLineSegment(sketch, "E274", {"start": v(99.92, -294.86) * mm, "end": v(99.92, -302.46) * mm});
            skLineSegment(sketch, "E275", {"start": v(99.92, -302.46) * mm, "end": v(99.92, -474.86) * mm});
            skLineSegment(sketch, "E276", {"start": v(99.92, -474.86) * mm, "end": v(99.92, -482.46) * mm});
            skArc(sketch, "E277", {"start": v(93.62, -302.46) * mm, "mid": v(91.4, -297.09) * mm, "end": v(86.02, -294.86) * mm});
            skArc(sketch, "E278", {"start": v(107.8, -294.86) * mm, "mid": v(102.24, -296.99) * mm, "end": v(99.92, -302.46) * mm});
            skArc(sketch, "E279", {"start": v(93.62, -474.86) * mm, "mid": v(91.4, -480.24) * mm, "end": v(86.02, -482.46) * mm});
            skArc(sketch, "E280", {"start": v(99.92, -474.86) * mm, "mid": v(102.34, -480.43) * mm, "end": v(108.07, -482.46) * mm});
            skLineSegment(sketch, "E281", {"start": v(107.8, -294.86) * mm, "end": v(163.67, -294.86) * mm});
            skSolve(sketch);
        }
        {
            var Q0;
            Q0=makeQuery(id+"F52.imprint","IMPRINT",FACE,{"disambiguationData":[TD([[makeQuery(id+"F52.imprint","IMPRINT",EDGE,{"derivedFrom":sQuery(id+"F52.wireOp",EDGE,"E261")}),-1.0]])]});
            var Q1;
            {var subQ0=sQuery(id+"F52.wireOp",EDGE,"E271");Q1=makeQuery(id+"F52.imprint","IMPRINT",FACE,{"disambiguationData":[TD([[makeQuery(id+"F52.imprint","IMPRINT",EDGE,{"derivedFrom":subQ0}),-1.0]])]});}
            var Q2;
            {var subQ0=sQuery(id+"F52.wireOp",EDGE,"E273");Q2=makeQuery(id+"F52.imprint","IMPRINT",FACE,{"disambiguationData":[TD([[makeQuery(id+"F52.imprint","IMPRINT",EDGE,{"derivedFrom":subQ0}),-1.0]])]});}
            var Q3;
            {var subQ0=sQuery(id+"F52.wireOp",EDGE,"E274");Q3=makeQuery(id+"F52.imprint","IMPRINT",FACE,{"disambiguationData":[TD([[makeQuery(id+"F52.imprint","IMPRINT",EDGE,{"derivedFrom":subQ0}),1.0]])]});}
            var Q4;
            {var subQ0=sQuery(id+"F52.wireOp",EDGE,"E280");var subQ1=sQuery(id+"F52.wireOp",EDGE,"E270");var subQ2=makeQuery(id+"F52.imprint","INTERSECT",VERTEX,{"disambiguationData":[OD(0.0)],"derivedFrom":[subQ1,subQ0]});Q4=makeQuery(id+"F52.imprint","IMPRINT",FACE,{"disambiguationData":[TD([[makeQuery(id+"F52.imprint","IMPRINT",EDGE,{"disambiguationData":[TD([[subQ2,-1.0]])],"derivedFrom":subQ1}),1.0]])]});}
            var Q5;
            {var subQ0=sQuery(id+"F52.wireOp",EDGE,"E276");Q5=makeQuery(id+"F52.imprint","IMPRINT",FACE,{"disambiguationData":[TD([[makeQuery(id+"F52.imprint","IMPRINT",EDGE,{"derivedFrom":subQ0}),1.0]])]});}
            var Q6;
            {var subQ0=sQuery(id+"F52.wireOp",EDGE,"E278");var subQ1=sQuery(id+"F52.wireOp",EDGE,"E265");var subQ3=makeQuery(id+"F52.imprint","INTERSECT",VERTEX,{"derivedFrom":[subQ1,subQ0]});Q6=makeQuery(id+"F52.imprint","IMPRINT",FACE,{"disambiguationData":[TD([[makeQuery(id+"F52.imprint","IMPRINT",EDGE,{"disambiguationData":[TD([[subQ3,1.0]])],"derivedFrom":subQ1}),-1.0]])]});}
            extrude(context, id + "F53", {"entities" : qUnion([Q0, Q1, Q2, Q3, Q4, Q5, Q6]), "depth" : 1830 * mm});
        }
        {
            var Q0;
            Q0=makeQuery(id+"F53.opExtrude","SWEPT_FACE",FACE,{"disambiguationData":[OSD([sQuery(id+"F52.wireOp",EDGE,"E261")])]});
            var sketch = newSketch(context, id + "F54", { "sketchPlane" : qUnion([Q0])});
            skLineSegment(sketch, "E282", {"start": v(29.87, -915) * mm, "end": v(163.67, -915) * mm, "construction": true});
            skLineSegment(sketch, "E283.bottom", {"start": v(29.87, -1830) * mm, "end": v(163.67, -1830) * mm});
            skLineSegment(sketch, "E283.top", {"start": v(29.87, -1766.25) * mm, "end": v(163.67, -1766.25) * mm});
            skLineSegment(sketch, "E283.left", {"start": v(29.87, -1830) * mm, "end": v(29.87, -1766.25) * mm});
            skLineSegment(sketch, "E283.right", {"start": v(163.67, -1830) * mm, "end": v(163.67, -1766.25) * mm});
            skLineSegment(sketch, "E284.MirrorCS", {"start": v(29.87, 0) * mm, "end": v(29.87, -63.75) * mm});
            skLineSegment(sketch, "E285.MirrorCS", {"start": v(163.67, 0) * mm, "end": v(163.67, -63.75) * mm});
            skLineSegment(sketch, "E286.MirrorCS", {"start": v(29.87, -63.75) * mm, "end": v(163.67, -63.75) * mm});
            skLineSegment(sketch, "E287.MirrorCS", {"start": v(29.87, 0) * mm, "end": v(163.67, 0) * mm});
            skSolve(sketch);
        }
        {
            var Q0;
            Q0=makeQuery(id+"F54.imprint","IMPRINT",FACE,{"disambiguationData":[TD([[makeQuery(id+"F54.imprint","IMPRINT",EDGE,{"derivedFrom":sQuery(id+"F54.wireOp",EDGE,"E284.MirrorCS")}),-1.0]])]});
            var Q1;
            Q1=makeQuery(id+"F54.imprint","IMPRINT",FACE,{"disambiguationData":[TD([[makeQuery(id+"F54.imprint","IMPRINT",EDGE,{"derivedFrom":sQuery(id+"F54.wireOp",EDGE,"E283.bottom")}),1.0]])]});
            extrude(context, id + "F55", {"entities" : qUnion([Q0, Q1]), "operationType" : NewBodyOperationType.REMOVE, "oppositeDirection" : true, "depth" : 25 * mm});
        }
        {
            var Q0;
            Q0=makeQuery(id+"F53.opExtrude","SWEPT_FACE",FACE,{"disambiguationData":[OSD([sQuery(id+"F52.wireOp",EDGE,"E268")])]});
            var sketch = newSketch(context, id + "F56", { "sketchPlane" : qUnion([Q0])});
            skLineSegment(sketch, "E288.bottom", {"start": v(29.87, 0) * mm, "end": v(163.67, 0) * mm});
            skLineSegment(sketch, "E288.top", {"start": v(29.87, 63.75) * mm, "end": v(163.67, 63.75) * mm});
            skLineSegment(sketch, "E288.left", {"start": v(29.87, 0) * mm, "end": v(29.87, 63.75) * mm});
            skLineSegment(sketch, "E288.right", {"start": v(163.67, 0) * mm, "end": v(163.67, 63.75) * mm});
            skLineSegment(sketch, "E289", {"start": v(29.87, 915) * mm, "end": v(163.67, 915) * mm});
            skLineSegment(sketch, "E290.MirrorCS", {"start": v(163.67, 1830) * mm, "end": v(163.67, 1766.25) * mm});
            skLineSegment(sketch, "E291.MirrorCS", {"start": v(29.87, 1830) * mm, "end": v(29.87, 1766.25) * mm});
            skLineSegment(sketch, "E292.MirrorCS", {"start": v(29.87, 1830) * mm, "end": v(163.67, 1830) * mm});
            skLineSegment(sketch, "E293.MirrorCS", {"start": v(29.87, 1766.25) * mm, "end": v(163.67, 1766.25) * mm});
            skSolve(sketch);
        }
        {
            var Q0;
            Q0 = qSketchRegion(id + "F56", true);
            extrude(context, id + "F57", {"entities" : qUnion([Q0]), "operationType" : NewBodyOperationType.REMOVE, "oppositeDirection" : true, "depth" : 25 * mm});
        }
        {
            var Q0;
            Q0=makeQuery(id+"F34.imprint","IMPRINT",FACE,{"disambiguationData":[TD([[makeQuery(id+"F34.imprint","IMPRINT",EDGE,{"derivedFrom":sQuery(id+"F34.wireOp",EDGE,"E181.bottom")}),-1.0]])]});
            var Q1;
            Q1=makeQuery(id+"F34.imprint","IMPRINT",FACE,{"disambiguationData":[TD([[makeQuery(id+"F34.imprint","IMPRINT",EDGE,{"derivedFrom":sQuery(id+"F34.wireOp",EDGE,"E182.MirrorCS")}),-1.0]])]});
            extrude(context, id + "F58", {"entities" : qUnion([Q0, Q1]), "operationType" : NewBodyOperationType.REMOVE, "oppositeDirection" : true, "depth" : 25 * mm});
        }
        {
            var Q0;
            Q0=makeQuery(id+"F23.opExtrude","SWEPT_FACE",FACE,{"disambiguationData":[OSD([sQuery(id+"F22.wireOp",EDGE,"E106")])]});
            var sketch = newSketch(context, id + "F59", { "sketchPlane" : qUnion([Q0])});
            skLineSegment(sketch, "E294.bottom", {"start": v(725.07, 4898) * mm, "end": v(858.87, 4898) * mm});
            skLineSegment(sketch, "E294.top", {"start": v(725.07, 4834) * mm, "end": v(858.87, 4834) * mm});
            skLineSegment(sketch, "E294.left", {"start": v(725.07, 4898) * mm, "end": v(725.07, 4834) * mm});
            skLineSegment(sketch, "E294.right", {"start": v(858.87, 4898) * mm, "end": v(858.87, 4834) * mm});
            skLineSegment(sketch, "E295", {"start": v(725.07, 2449) * mm, "end": v(858.87, 2449) * mm, "construction": true});
            skLineSegment(sketch, "E296.MirrorCS", {"start": v(725.07, 0) * mm, "end": v(725.07, 64) * mm});
            skLineSegment(sketch, "E297.MirrorCS", {"start": v(725.07, 0) * mm, "end": v(858.87, 0) * mm});
            skLineSegment(sketch, "E298.MirrorCS", {"start": v(858.87, 0) * mm, "end": v(858.87, 64) * mm});
            skLineSegment(sketch, "E299.MirrorCS", {"start": v(725.07, 64) * mm, "end": v(858.87, 64) * mm});
            skSolve(sketch);
        }
        {
            var Q0;
            Q0 = qSketchRegion(id + "F59", true);
            extrude(context, id + "F60", {"entities" : qUnion([Q0]), "operationType" : NewBodyOperationType.REMOVE, "oppositeDirection" : true, "depth" : 25 * mm});
        }
        {
            var Q0;
            Q0=makeQuery(id+"F23.opExtrude","SWEPT_FACE",FACE,{"disambiguationData":[OSD([sQuery(id+"F22.wireOp",EDGE,"E113")])]});
            var sketch = newSketch(context, id + "F61", { "sketchPlane" : qUnion([Q0])});
            skLineSegment(sketch, "E300", {"start": v(-2449, 10.01) * mm, "end": v(-2449, 182.41) * mm});
            skLineSegment(sketch, "E301", {"start": v(-1199, 10.01) * mm, "end": v(-1199, 182.41) * mm});
            skLineSegment(sketch, "E302", {"start": v(-3699, 10.01) * mm, "end": v(-3699, 182.41) * mm});
            skSolve(sketch);
        }
        {
            var Q0;
            Q0=makeQuery(id+"F7.opExtrude","SWEPT_FACE",FACE,{"disambiguationData":[OSD([sQuery(id+"F6.wireOp",EDGE,"E39")])]});
            var sketch = newSketch(context, id + "F62", { "sketchPlane" : qUnion([Q0])});
            skLineSegment(sketch, "E303", {"start": v(-2000, -48.3) * mm, "end": v(-2000, 124.1) * mm});
            skLineSegment(sketch, "E304", {"start": v(-164, -48.3) * mm, "end": v(-164, 124.1) * mm});
            skLineSegment(sketch, "E305", {"start": v(-3836, -48.3) * mm, "end": v(-3836, 124.1) * mm});
            skSolve(sketch);
        }
    });
